# Revit family: equip-water-cooler-hlsy-tylr-hthb-w
name_source: partatom
category: Plumbing Fixtures
units: mm (PartAtom-declared; Revit-internal decimal feet)

## family parameters
Always vertical = Yes
Cut with Voids When Loaded = No
OmniClass Number = 23.45.00.00
OmniClass Title = Sanitary, Laundry, and Cleaning Equipment
Part Type = Normal
Room Calculation Point = No
Round Connector Dimension = Use Radius
Shared = No
Work Plane-Based = No

## types (1)
- equip-water-cooler-hlsy-tylr-hthb-w
    Apparent Load Phase 1 = 0 VA
    Body Material = Metal - Steel - Stainless - Chrome
    Chiller Option = Yes
    Description = Recessed Bottle Filling Station
    Manufacturer = Halsey Taylor
    Model = HTHB-HAC-RF-NF
    Number of Poles = 1
    Plan-View = Yes
    Plastic One Material = Metal - Steel - Stainless - Color 3
    Plastic Two Material = Metal - Steel - Stainless - Color 2
    Power Factor = 1
    Spec Sheet/Installation = http://www.halseytaylor.com
    URL = www.halseytaylor.com
    Voltage = 0 V
    Water Service Flow = 0 GPM
    Water Service Flow Out = 0 GPM
    Water Service Radius = 0' - 0 3/16"

## geometry (parser evidence)
native form markers: Sweep x12
no freeform markers — native parametric forms only
